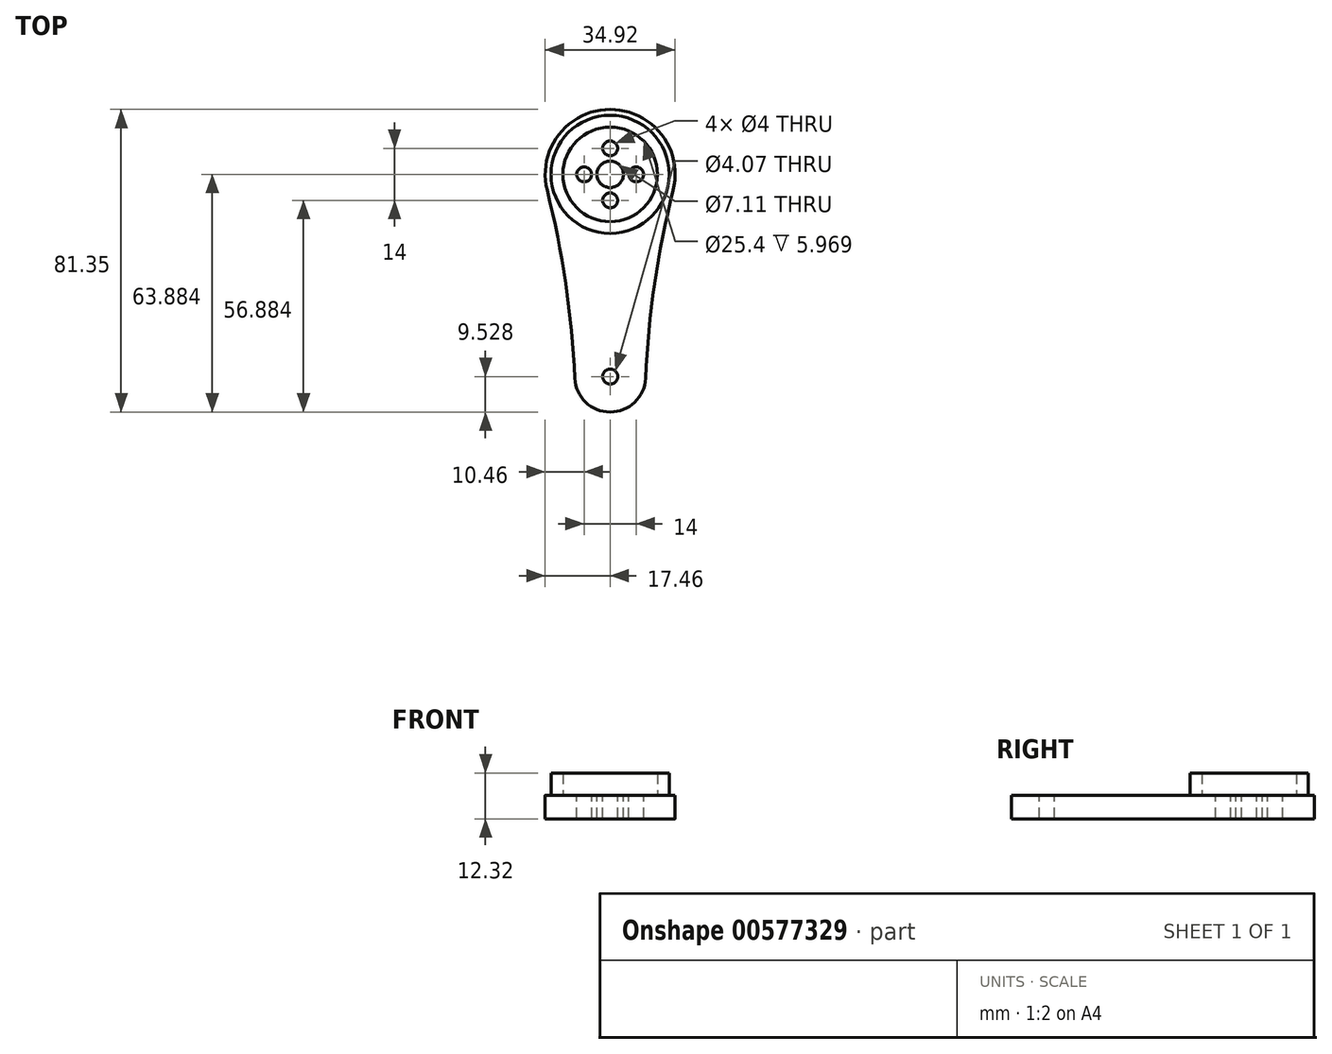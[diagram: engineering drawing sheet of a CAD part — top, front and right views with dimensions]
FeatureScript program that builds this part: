
annotation { "Feature Type Name" : "Feature", "Feature Type Description" : "" }
export const myFeature = defineFeature(function(context is Context, id is Id, definition is map)
    precondition{}
    {
        {
            var Q0;
            Q0=qCreatedBy(makeId("Top.planeOp"),FACE);
            var sketch = newSketch(context, id + "F0", { "sketchPlane" : qUnion([Q0])});
            skCircle(sketch, "E0", {"center": v(0, -31.2) * mm, "radius": 2.03 * mm});
            skCircle(sketch, "E1", {"center": v(0, 23.16) * mm, "radius": 3.56 * mm});
            skArc(sketch, "E2", {"start": v(16.93, 18.9) * mm, "mid": v(0, 40.63) * mm, "end": v(-16.93, 18.9) * mm});
            skArc(sketch, "E3", {"start": v(-9.52, -31.62) * mm, "mid": v(-11.95, -6.17) * mm, "end": v(-16.93, 18.9) * mm});
            skArc(sketch, "E4", {"start": v(16.93, 18.9) * mm, "mid": v(11.95, -6.17) * mm, "end": v(9.52, -31.62) * mm});
            skArc(sketch, "E5", {"start": v(-9.52, -31.62) * mm, "mid": v(0, -40.72) * mm, "end": v(9.52, -31.62) * mm});
            skCircle(sketch, "E6", {"center": v(0, 30.16) * mm, "radius": 2 * mm});
            skCircle(sketch, "E7.1.0", {"center": v(-7, 23.16) * mm, "radius": 2 * mm});
            skCircle(sketch, "E7.2.0", {"center": v(0, 16.16) * mm, "radius": 2 * mm});
            skCircle(sketch, "E7.3.0", {"center": v(7, 23.16) * mm, "radius": 2 * mm});
            skSolve(sketch);
        }
        {
            var Q0;
            Q0 = qSketchRegion(id + "F0", true);
            extrude(context, id + "F1", {"entities" : qUnion([Q0]), "oppositeDirection" : true, "depth" : 6.35 * mm, "offsetDistance" : 25.4 * mm});
        }
        {
            var Q0;
            Q0=makeQuery(id+"F1.opExtrude","CAP_FACE",FACE,{"disambiguationData":[OSD([sQuery(id+"F0.wireOp",EDGE,"E0"),sQuery(id+"F0.wireOp",EDGE,"E1"),sQuery(id+"F0.wireOp",EDGE,"E2"),sQuery(id+"F0.wireOp",EDGE,"E3"),sQuery(id+"F0.wireOp",EDGE,"E4"),sQuery(id+"F0.wireOp",EDGE,"E5"),sQuery(id+"F0.wireOp",EDGE,"E6"),sQuery(id+"F0.wireOp",EDGE,"E7.1.0"),sQuery(id+"F0.wireOp",EDGE,"E7.2.0"),sQuery(id+"F0.wireOp",EDGE,"E7.3.0")])],"isStart":true});
            var sketch = newSketch(context, id + "F2", { "sketchPlane" : qUnion([Q0])});
            skCircle(sketch, "E8", {"center": v(0, 23.16) * mm, "radius": 15.88 * mm});
            skCircle(sketch, "E9", {"center": v(0, 23.16) * mm, "radius": 12.7 * mm});
            skSolve(sketch);
        }
        {
            var Q0;
            Q0 = qSketchRegion(id + "F2", true);
            extrude(context, id + "F3", {"entities" : qUnion([Q0]), "operationType" : NewBodyOperationType.ADD, "depth" : 5.97 * mm, "offsetDistance" : 25.4 * mm});
        }
    });
